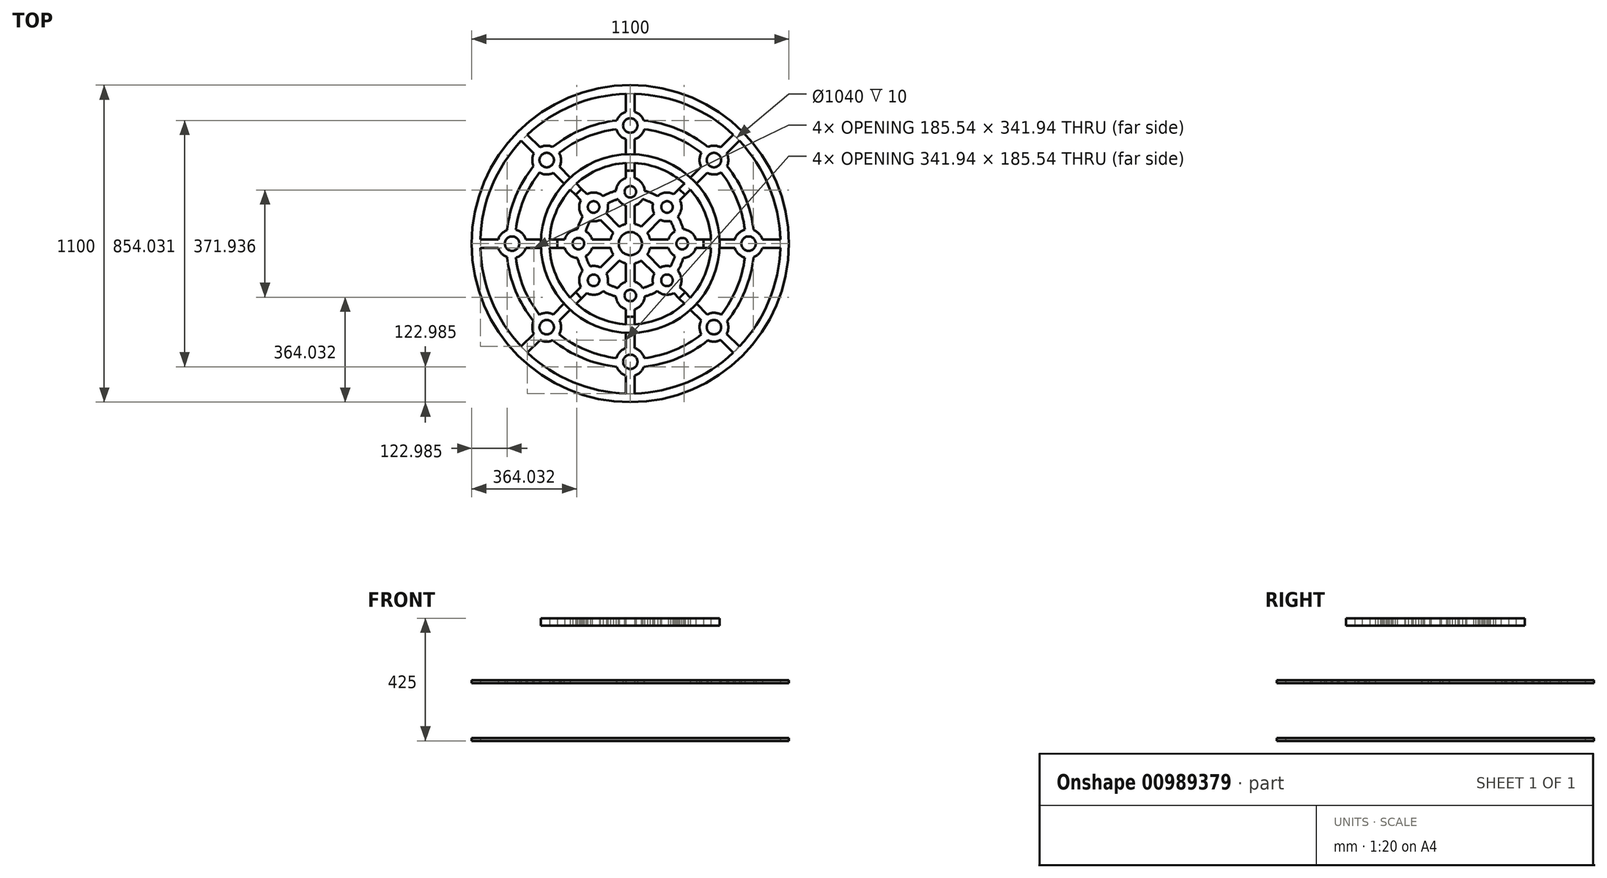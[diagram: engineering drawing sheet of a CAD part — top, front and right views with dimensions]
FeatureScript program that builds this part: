
annotation { "Feature Type Name" : "Feature", "Feature Type Description" : "" }
export const myFeature = defineFeature(function(context is Context, id is Id, definition is map)
    precondition{}
    {
        {
            var Q0;
            Q0=qCreatedBy(makeId("Top.planeOp"),FACE);
            cPlane(context, id + "F0", {"entities" : qUnion([Q0]), "cplaneType" : CPlaneType.OFFSET, "offset" : 200 * mm, "width" : 150 * mm, "height" : 150 * mm});
        }
        {
            var Q0;
            Q0=qCreatedBy(makeId("Top.planeOp"),FACE);
            cPlane(context, id + "F1", {"entities" : qUnion([Q0]), "cplaneType" : CPlaneType.OFFSET, "offset" : 200 * mm, "oppositeDirection" : true, "width" : 150 * mm, "height" : 150 * mm});
        }
        {
            var Q0;
            Q0=qCreatedBy(makeId("Top.planeOp"),FACE);
            var sketch = newSketch(context, id + "F2", { "sketchPlane" : qUnion([Q0])});
            skCircle(sketch, "E0", {"center": v(0, 0) * mm, "radius": 550 * mm});
            skArc(sketch, "E1", {"start": v(15, -519.78) * mm, "mid": v(199, -480.42) * mm, "end": v(356.94, -378.15) * mm});
            skArc(sketch, "E2", {"start": v(46.86, -427.44) * mm, "mid": v(164.55, -397.27) * mm, "end": v(269.1, -335.38) * mm});
            skArc(sketch, "E3", {"start": v(48.3, -397.07) * mm, "mid": v(153.07, -369.55) * mm, "end": v(246.62, -314.93) * mm});
            skArc(sketch, "E4", {"start": v(15, -309.64) * mm, "mid": v(118.63, -286.4) * mm, "end": v(208.34, -229.55) * mm});
            skCircle(sketch, "E5", {"center": v(0, 0) * mm, "radius": 280 * mm});
            skCircle(sketch, "E6", {"center": v(0, 0) * mm, "radius": 190 * mm, "construction": true});
            skCircle(sketch, "E7", {"center": v(0, 0) * mm, "radius": 160 * mm, "construction": true});
            skCircle(sketch, "E8", {"center": v(0, 0) * mm, "radius": 40 * mm, "construction": true});
            skCircle(sketch, "E9", {"center": v(0, 0) * mm, "radius": 70 * mm, "construction": true});
            skLineSegment(sketch, "E10", {"start": v(0, 725.48) * mm, "end": v(0, -722.46) * mm, "construction": true});
            skLineSegment(sketch, "E11", {"start": v(-695.44, 0) * mm, "end": v(901.66, 0) * mm, "construction": true});
            skArc(sketch, "E12", {"start": v(-15, -362.3) * mm, "mid": v(-36.11, -375.42) * mm, "end": v(-48.3, -397.07) * mm});
            skCircle(sketch, "E13", {"center": v(0, -410) * mm, "radius": 25 * mm});
            skLineSegment(sketch, "E14", {"start": v(15, -519.78) * mm, "end": v(15, -457.7) * mm});
            skLineSegment(sketch, "E15", {"start": v(-15, -457.7) * mm, "end": v(-15, -519.78) * mm});
            skLineSegment(sketch, "E16", {"start": v(-15, -362.3) * mm, "end": v(-15, -309.64) * mm});
            skLineSegment(sketch, "E17", {"start": v(15, -362.3) * mm, "end": v(15, -309.64) * mm});
            skArc(sketch, "E18.trimOffspring", {"start": v(-46.86, -427.44) * mm, "mid": v(-34.43, -446.26) * mm, "end": v(-15, -457.7) * mm});
            skArc(sketch, "E19.trimOffspring", {"start": v(48.3, -397.07) * mm, "mid": v(36.11, -375.42) * mm, "end": v(15, -362.3) * mm});
            skArc(sketch, "E20.trimOffspring", {"start": v(15, -457.7) * mm, "mid": v(34.43, -446.26) * mm, "end": v(46.86, -427.44) * mm});
            skArc(sketch, "E21.1.0", {"start": v(334.25, -313.03) * mm, "mid": v(339.9, -291.2) * mm, "end": v(335.38, -269.1) * mm});
            skCircle(sketch, "E21.1.1", {"center": v(289.91, -289.91) * mm, "radius": 25 * mm});
            skLineSegment(sketch, "E21.1.2", {"start": v(266.8, -245.58) * mm, "end": v(229.55, -208.34) * mm});
            skLineSegment(sketch, "E21.1.3", {"start": v(245.58, -266.8) * mm, "end": v(208.34, -229.55) * mm});
            skArc(sketch, "E21.1.4", {"start": v(245.58, -266.8) * mm, "mid": v(239.93, -291) * mm, "end": v(246.62, -314.93) * mm});
            skArc(sketch, "E21.1.5", {"start": v(269.1, -335.38) * mm, "mid": v(291.2, -339.9) * mm, "end": v(313.03, -334.25) * mm});
            skArc(sketch, "E21.1.6", {"start": v(314.93, -246.62) * mm, "mid": v(291, -239.93) * mm, "end": v(266.8, -245.58) * mm});
            skLineSegment(sketch, "E21.1.7", {"start": v(378.15, -356.94) * mm, "end": v(334.25, -313.03) * mm});
            skLineSegment(sketch, "E21.1.8", {"start": v(313.03, -334.25) * mm, "end": v(356.94, -378.15) * mm});
            skArc(sketch, "E21.2.0", {"start": v(457.7, 15) * mm, "mid": v(446.26, 34.43) * mm, "end": v(427.44, 46.86) * mm});
            skCircle(sketch, "E21.2.1", {"center": v(410, 0) * mm, "radius": 25 * mm});
            skLineSegment(sketch, "E21.2.2", {"start": v(362.3, 15) * mm, "end": v(309.64, 15) * mm});
            skLineSegment(sketch, "E21.2.3", {"start": v(362.3, -15) * mm, "end": v(309.64, -15) * mm});
            skArc(sketch, "E21.2.4", {"start": v(362.3, -15) * mm, "mid": v(375.42, -36.11) * mm, "end": v(397.07, -48.3) * mm});
            skArc(sketch, "E21.2.5", {"start": v(427.44, -46.86) * mm, "mid": v(446.26, -34.43) * mm, "end": v(457.7, -15) * mm});
            skArc(sketch, "E21.2.6", {"start": v(397.07, 48.3) * mm, "mid": v(375.42, 36.11) * mm, "end": v(362.3, 15) * mm});
            skLineSegment(sketch, "E21.2.7", {"start": v(519.78, 15) * mm, "end": v(457.7, 15) * mm});
            skLineSegment(sketch, "E21.2.8", {"start": v(457.7, -15) * mm, "end": v(519.78, -15) * mm});
            skArc(sketch, "E21.3.0", {"start": v(313.03, 334.25) * mm, "mid": v(291.2, 339.9) * mm, "end": v(269.1, 335.38) * mm});
            skCircle(sketch, "E21.3.1", {"center": v(289.91, 289.91) * mm, "radius": 25 * mm});
            skLineSegment(sketch, "E21.3.2", {"start": v(245.58, 266.8) * mm, "end": v(208.34, 229.55) * mm});
            skLineSegment(sketch, "E21.3.3", {"start": v(266.8, 245.58) * mm, "end": v(229.55, 208.34) * mm});
            skArc(sketch, "E21.3.4", {"start": v(266.8, 245.58) * mm, "mid": v(291, 239.93) * mm, "end": v(314.93, 246.62) * mm});
            skArc(sketch, "E21.3.5", {"start": v(335.38, 269.1) * mm, "mid": v(339.9, 291.2) * mm, "end": v(334.25, 313.03) * mm});
            skArc(sketch, "E21.3.6", {"start": v(246.62, 314.93) * mm, "mid": v(239.93, 291) * mm, "end": v(245.58, 266.8) * mm});
            skLineSegment(sketch, "E21.3.7", {"start": v(356.94, 378.15) * mm, "end": v(313.03, 334.25) * mm});
            skLineSegment(sketch, "E21.3.8", {"start": v(334.25, 313.03) * mm, "end": v(378.15, 356.94) * mm});
            skArc(sketch, "E21.4.0", {"start": v(-15, 457.7) * mm, "mid": v(-34.43, 446.26) * mm, "end": v(-46.86, 427.44) * mm});
            skCircle(sketch, "E21.4.1", {"center": v(0, 410) * mm, "radius": 25 * mm});
            skLineSegment(sketch, "E21.4.2", {"start": v(-15, 362.3) * mm, "end": v(-15, 309.64) * mm});
            skLineSegment(sketch, "E21.4.3", {"start": v(15, 362.3) * mm, "end": v(15, 309.64) * mm});
            skArc(sketch, "E21.4.4", {"start": v(15, 362.3) * mm, "mid": v(36.11, 375.42) * mm, "end": v(48.3, 397.07) * mm});
            skArc(sketch, "E21.4.5", {"start": v(46.86, 427.44) * mm, "mid": v(34.43, 446.26) * mm, "end": v(15, 457.7) * mm});
            skArc(sketch, "E21.4.6", {"start": v(-48.3, 397.07) * mm, "mid": v(-36.11, 375.42) * mm, "end": v(-15, 362.3) * mm});
            skLineSegment(sketch, "E21.4.7", {"start": v(-15, 519.78) * mm, "end": v(-15, 457.7) * mm});
            skLineSegment(sketch, "E21.4.8", {"start": v(15, 457.7) * mm, "end": v(15, 519.78) * mm});
            skArc(sketch, "E21.5.0", {"start": v(-334.25, 313.03) * mm, "mid": v(-339.9, 291.2) * mm, "end": v(-335.38, 269.1) * mm});
            skCircle(sketch, "E21.5.1", {"center": v(-289.91, 289.91) * mm, "radius": 25 * mm});
            skLineSegment(sketch, "E21.5.2", {"start": v(-266.8, 245.58) * mm, "end": v(-229.55, 208.34) * mm});
            skLineSegment(sketch, "E21.5.3", {"start": v(-245.58, 266.8) * mm, "end": v(-208.34, 229.55) * mm});
            skArc(sketch, "E21.5.4", {"start": v(-245.58, 266.8) * mm, "mid": v(-239.93, 291) * mm, "end": v(-246.62, 314.93) * mm});
            skArc(sketch, "E21.5.5", {"start": v(-269.1, 335.38) * mm, "mid": v(-291.2, 339.9) * mm, "end": v(-313.03, 334.25) * mm});
            skArc(sketch, "E21.5.6", {"start": v(-314.93, 246.62) * mm, "mid": v(-291, 239.93) * mm, "end": v(-266.8, 245.58) * mm});
            skLineSegment(sketch, "E21.5.7", {"start": v(-378.15, 356.94) * mm, "end": v(-334.25, 313.03) * mm});
            skLineSegment(sketch, "E21.5.8", {"start": v(-313.03, 334.25) * mm, "end": v(-356.94, 378.15) * mm});
            skArc(sketch, "E21.6.0", {"start": v(-457.7, -15) * mm, "mid": v(-446.26, -34.43) * mm, "end": v(-427.44, -46.86) * mm});
            skCircle(sketch, "E21.6.1", {"center": v(-410, 0) * mm, "radius": 25 * mm});
            skLineSegment(sketch, "E21.6.2", {"start": v(-362.3, -15) * mm, "end": v(-309.64, -15) * mm});
            skLineSegment(sketch, "E21.6.3", {"start": v(-362.3, 15) * mm, "end": v(-309.64, 15) * mm});
            skArc(sketch, "E21.6.4", {"start": v(-362.3, 15) * mm, "mid": v(-375.42, 36.11) * mm, "end": v(-397.07, 48.3) * mm});
            skArc(sketch, "E21.6.5", {"start": v(-427.44, 46.86) * mm, "mid": v(-446.26, 34.43) * mm, "end": v(-457.7, 15) * mm});
            skArc(sketch, "E21.6.6", {"start": v(-397.07, -48.3) * mm, "mid": v(-375.42, -36.11) * mm, "end": v(-362.3, -15) * mm});
            skLineSegment(sketch, "E21.6.7", {"start": v(-519.78, -15) * mm, "end": v(-457.7, -15) * mm});
            skLineSegment(sketch, "E21.6.8", {"start": v(-457.7, 15) * mm, "end": v(-519.78, 15) * mm});
            skArc(sketch, "E21.7.0", {"start": v(-313.03, -334.25) * mm, "mid": v(-291.2, -339.9) * mm, "end": v(-269.1, -335.38) * mm});
            skCircle(sketch, "E21.7.1", {"center": v(-289.91, -289.91) * mm, "radius": 25 * mm});
            skLineSegment(sketch, "E21.7.2", {"start": v(-245.58, -266.8) * mm, "end": v(-208.34, -229.55) * mm});
            skLineSegment(sketch, "E21.7.3", {"start": v(-266.8, -245.58) * mm, "end": v(-229.55, -208.34) * mm});
            skArc(sketch, "E21.7.4", {"start": v(-266.8, -245.58) * mm, "mid": v(-291, -239.93) * mm, "end": v(-314.93, -246.62) * mm});
            skArc(sketch, "E21.7.5", {"start": v(-335.38, -269.1) * mm, "mid": v(-339.9, -291.2) * mm, "end": v(-334.25, -313.03) * mm});
            skArc(sketch, "E21.7.6", {"start": v(-246.62, -314.93) * mm, "mid": v(-239.93, -291) * mm, "end": v(-245.58, -266.8) * mm});
            skLineSegment(sketch, "E21.7.7", {"start": v(-356.94, -378.15) * mm, "end": v(-313.03, -334.25) * mm});
            skLineSegment(sketch, "E21.7.8", {"start": v(-334.25, -313.03) * mm, "end": v(-378.15, -356.94) * mm});
            skArc(sketch, "E22.trimOffspring", {"start": v(-246.62, -314.93) * mm, "mid": v(-153.07, -369.55) * mm, "end": v(-48.3, -397.07) * mm});
            skArc(sketch, "E23.trimOffspring", {"start": v(-269.1, -335.38) * mm, "mid": v(-164.55, -397.27) * mm, "end": v(-46.86, -427.44) * mm});
            skArc(sketch, "E24.trimOffspring", {"start": v(-356.94, -378.15) * mm, "mid": v(-199, -480.42) * mm, "end": v(-15, -519.78) * mm});
            skArc(sketch, "E25.trimOffspring", {"start": v(-208.34, -229.55) * mm, "mid": v(-118.63, -286.4) * mm, "end": v(-15, -309.64) * mm});
            skArc(sketch, "E26.trimOffspring", {"start": v(-397.07, -48.3) * mm, "mid": v(-369.55, -153.07) * mm, "end": v(-314.93, -246.62) * mm});
            skArc(sketch, "E27.trimOffspring", {"start": v(-427.44, -46.86) * mm, "mid": v(-397.27, -164.55) * mm, "end": v(-335.38, -269.1) * mm});
            skArc(sketch, "E28.trimOffspring", {"start": v(-309.64, -15) * mm, "mid": v(-286.4, -118.63) * mm, "end": v(-229.55, -208.34) * mm});
            skArc(sketch, "E29.trimOffspring", {"start": v(-519.78, -15) * mm, "mid": v(-480.42, -199) * mm, "end": v(-378.15, -356.94) * mm});
            skArc(sketch, "E30.trimOffspring", {"start": v(-314.93, 246.62) * mm, "mid": v(-369.55, 153.07) * mm, "end": v(-397.07, 48.3) * mm});
            skArc(sketch, "E31.trimOffspring", {"start": v(-335.38, 269.1) * mm, "mid": v(-397.27, 164.55) * mm, "end": v(-427.44, 46.86) * mm});
            skArc(sketch, "E32.trimOffspring", {"start": v(-378.15, 356.94) * mm, "mid": v(-480.42, 199) * mm, "end": v(-519.78, 15) * mm});
            skArc(sketch, "E33.trimOffspring", {"start": v(-229.55, 208.34) * mm, "mid": v(-286.4, 118.63) * mm, "end": v(-309.64, 15) * mm});
            skArc(sketch, "E34.trimOffspring", {"start": v(-15, 309.64) * mm, "mid": v(-118.63, 286.4) * mm, "end": v(-208.34, 229.55) * mm});
            skArc(sketch, "E35.trimOffspring", {"start": v(-48.3, 397.07) * mm, "mid": v(-153.07, 369.55) * mm, "end": v(-246.62, 314.93) * mm});
            skArc(sketch, "E36.trimOffspring", {"start": v(-46.86, 427.44) * mm, "mid": v(-164.55, 397.27) * mm, "end": v(-269.1, 335.38) * mm});
            skArc(sketch, "E37.trimOffspring", {"start": v(-15, 519.78) * mm, "mid": v(-199, 480.42) * mm, "end": v(-356.94, 378.15) * mm});
            skArc(sketch, "E38.trimOffspring", {"start": v(269.1, 335.38) * mm, "mid": v(164.55, 397.27) * mm, "end": v(46.86, 427.44) * mm});
            skArc(sketch, "E39.trimOffspring", {"start": v(246.62, 314.93) * mm, "mid": v(153.07, 369.55) * mm, "end": v(48.3, 397.07) * mm});
            skArc(sketch, "E40.trimOffspring", {"start": v(208.34, 229.55) * mm, "mid": v(118.63, 286.4) * mm, "end": v(15, 309.64) * mm});
            skArc(sketch, "E41.trimOffspring", {"start": v(356.94, 378.15) * mm, "mid": v(199, 480.42) * mm, "end": v(15, 519.78) * mm});
            skArc(sketch, "E42.trimOffspring", {"start": v(309.64, 15) * mm, "mid": v(286.4, 118.63) * mm, "end": v(229.55, 208.34) * mm});
            skArc(sketch, "E43.trimOffspring", {"start": v(397.07, 48.3) * mm, "mid": v(369.55, 153.07) * mm, "end": v(314.93, 246.62) * mm});
            skArc(sketch, "E44.trimOffspring", {"start": v(427.44, 46.86) * mm, "mid": v(397.27, 164.55) * mm, "end": v(335.38, 269.1) * mm});
            skArc(sketch, "E45.trimOffspring", {"start": v(519.78, 15) * mm, "mid": v(480.42, 199) * mm, "end": v(378.15, 356.94) * mm});
            skArc(sketch, "E46.trimOffspring", {"start": v(335.38, -269.1) * mm, "mid": v(397.27, -164.55) * mm, "end": v(427.44, -46.86) * mm});
            skArc(sketch, "E47.trimOffspring", {"start": v(314.93, -246.62) * mm, "mid": v(369.55, -153.07) * mm, "end": v(397.07, -48.3) * mm});
            skArc(sketch, "E48.trimOffspring", {"start": v(378.15, -356.94) * mm, "mid": v(480.42, -199) * mm, "end": v(519.78, -15) * mm});
            skArc(sketch, "E49.trimOffspring", {"start": v(229.55, -208.34) * mm, "mid": v(286.4, -118.63) * mm, "end": v(309.64, -15) * mm});
            skSolve(sketch);
        }
        {
            var Q0;
            Q0 = qSketchRegion(id + "F2", true);
            extrude(context, id + "F3", {"entities" : qUnion([Q0]), "depth" : 10 * mm, "offsetDistance" : 25 * mm});
        }
        {
            var Q0;
            Q0=qCreatedBy(id+"F0.planeOp",FACE);
            var sketch = newSketch(context, id + "F4", { "sketchPlane" : qUnion([Q0])});
            skArc(sketch, "E50.0", {"start": v(42.8, -154.17) * mm, "mid": v(61.23, -147.82) * mm, "end": v(78.74, -139.28) * mm});
            skArc(sketch, "E51.0", {"start": v(49.89, -183.33) * mm, "mid": v(72.7, -175.54) * mm, "end": v(94.36, -164.91) * mm});
            skArc(sketch, "E52.0", {"start": v(15, -279.6) * mm, "mid": v(107.15, -258.69) * mm, "end": v(187.1, -208.31) * mm});
            skArc(sketch, "E53.0", {"start": v(15, -68.37) * mm, "mid": v(26.79, -64.67) * mm, "end": v(37.74, -58.95) * mm});
            skCircle(sketch, "E54.0", {"center": v(0, 0) * mm, "radius": 40 * mm});
            skPoint(sketch, "E55.0", {"position": v(15, 309.64) * mm});
            skCircle(sketch, "E56", {"center": v(0, 0) * mm, "radius": 310 * mm});
            skArc(sketch, "E57", {"start": v(-15, -132.3) * mm, "mid": v(-30.9, -140.7) * mm, "end": v(-42.8, -154.17) * mm});
            skCircle(sketch, "E58", {"center": v(0, -180) * mm, "radius": 20 * mm});
            skLineSegment(sketch, "E59", {"start": v(-15, -68.37) * mm, "end": v(-15, -132.3) * mm});
            skLineSegment(sketch, "E60", {"start": v(15, -68.37) * mm, "end": v(15, -132.3) * mm});
            skLineSegment(sketch, "E61", {"start": v(-15, -227.7) * mm, "end": v(-15, -279.6) * mm});
            skLineSegment(sketch, "E62", {"start": v(15, -227.7) * mm, "end": v(15, -279.6) * mm});
            skArc(sketch, "E63.trimOffspring", {"start": v(42.8, -154.17) * mm, "mid": v(30.9, -140.7) * mm, "end": v(15, -132.3) * mm});
            skArc(sketch, "E64.trimOffspring", {"start": v(15, -227.7) * mm, "mid": v(39.3, -210.9) * mm, "end": v(49.89, -183.33) * mm});
            skArc(sketch, "E65.trimOffspring", {"start": v(-49.89, -183.33) * mm, "mid": v(-39.3, -210.9) * mm, "end": v(-15, -227.7) * mm});
            skLineSegment(sketch, "E66.1.0", {"start": v(58.95, -37.74) * mm, "end": v(104.16, -82.95) * mm});
            skLineSegment(sketch, "E66.1.1", {"start": v(37.74, -58.95) * mm, "end": v(82.95, -104.16) * mm});
            skArc(sketch, "E66.1.2", {"start": v(82.95, -104.16) * mm, "mid": v(77.63, -121.34) * mm, "end": v(78.74, -139.28) * mm});
            skCircle(sketch, "E66.1.3", {"center": v(127.28, -127.28) * mm, "radius": 20 * mm});
            skArc(sketch, "E66.1.4", {"start": v(94.36, -164.91) * mm, "mid": v(121.34, -176.93) * mm, "end": v(150.4, -171.61) * mm});
            skArc(sketch, "E66.1.5", {"start": v(171.61, -150.4) * mm, "mid": v(176.93, -121.34) * mm, "end": v(164.91, -94.36) * mm});
            skArc(sketch, "E66.1.6", {"start": v(139.28, -78.74) * mm, "mid": v(121.34, -77.63) * mm, "end": v(104.16, -82.95) * mm});
            skLineSegment(sketch, "E66.1.7", {"start": v(171.61, -150.4) * mm, "end": v(208.31, -187.1) * mm});
            skLineSegment(sketch, "E66.1.8", {"start": v(150.4, -171.61) * mm, "end": v(187.1, -208.31) * mm});
            skLineSegment(sketch, "E66.2.0", {"start": v(68.37, 15) * mm, "end": v(132.3, 15) * mm});
            skLineSegment(sketch, "E66.2.1", {"start": v(68.37, -15) * mm, "end": v(132.3, -15) * mm});
            skArc(sketch, "E66.2.2", {"start": v(132.3, -15) * mm, "mid": v(140.7, -30.9) * mm, "end": v(154.17, -42.8) * mm});
            skCircle(sketch, "E66.2.3", {"center": v(180, 0) * mm, "radius": 20 * mm});
            skArc(sketch, "E66.2.4", {"start": v(183.33, -49.89) * mm, "mid": v(210.9, -39.3) * mm, "end": v(227.7, -15) * mm});
            skArc(sketch, "E66.2.5", {"start": v(227.7, 15) * mm, "mid": v(210.9, 39.3) * mm, "end": v(183.33, 49.89) * mm});
            skArc(sketch, "E66.2.6", {"start": v(154.17, 42.8) * mm, "mid": v(140.7, 30.9) * mm, "end": v(132.3, 15) * mm});
            skLineSegment(sketch, "E66.2.7", {"start": v(227.7, 15) * mm, "end": v(279.6, 15) * mm});
            skLineSegment(sketch, "E66.2.8", {"start": v(227.7, -15) * mm, "end": v(279.6, -15) * mm});
            skLineSegment(sketch, "E66.3.0", {"start": v(37.74, 58.95) * mm, "end": v(82.95, 104.16) * mm});
            skLineSegment(sketch, "E66.3.1", {"start": v(58.95, 37.74) * mm, "end": v(104.16, 82.95) * mm});
            skArc(sketch, "E66.3.2", {"start": v(104.16, 82.95) * mm, "mid": v(121.34, 77.63) * mm, "end": v(139.28, 78.74) * mm});
            skCircle(sketch, "E66.3.3", {"center": v(127.28, 127.28) * mm, "radius": 20 * mm});
            skArc(sketch, "E66.3.4", {"start": v(164.91, 94.36) * mm, "mid": v(176.93, 121.34) * mm, "end": v(171.61, 150.4) * mm});
            skArc(sketch, "E66.3.5", {"start": v(150.4, 171.61) * mm, "mid": v(121.34, 176.93) * mm, "end": v(94.36, 164.91) * mm});
            skArc(sketch, "E66.3.6", {"start": v(78.74, 139.28) * mm, "mid": v(77.63, 121.34) * mm, "end": v(82.95, 104.16) * mm});
            skLineSegment(sketch, "E66.3.7", {"start": v(150.4, 171.61) * mm, "end": v(187.1, 208.31) * mm});
            skLineSegment(sketch, "E66.3.8", {"start": v(171.61, 150.4) * mm, "end": v(208.31, 187.1) * mm});
            skLineSegment(sketch, "E66.4.0", {"start": v(-15, 68.37) * mm, "end": v(-15, 132.3) * mm});
            skLineSegment(sketch, "E66.4.1", {"start": v(15, 68.37) * mm, "end": v(15, 132.3) * mm});
            skArc(sketch, "E66.4.2", {"start": v(15, 132.3) * mm, "mid": v(30.9, 140.7) * mm, "end": v(42.8, 154.17) * mm});
            skCircle(sketch, "E66.4.3", {"center": v(0, 180) * mm, "radius": 20 * mm});
            skArc(sketch, "E66.4.4", {"start": v(49.89, 183.33) * mm, "mid": v(39.3, 210.9) * mm, "end": v(15, 227.7) * mm});
            skArc(sketch, "E66.4.5", {"start": v(-15, 227.7) * mm, "mid": v(-39.3, 210.9) * mm, "end": v(-49.89, 183.33) * mm});
            skArc(sketch, "E66.4.6", {"start": v(-42.8, 154.17) * mm, "mid": v(-30.9, 140.7) * mm, "end": v(-15, 132.3) * mm});
            skLineSegment(sketch, "E66.4.7", {"start": v(-15, 227.7) * mm, "end": v(-15, 279.6) * mm});
            skLineSegment(sketch, "E66.4.8", {"start": v(15, 227.7) * mm, "end": v(15, 279.6) * mm});
            skLineSegment(sketch, "E66.5.0", {"start": v(-58.95, 37.74) * mm, "end": v(-104.16, 82.95) * mm});
            skLineSegment(sketch, "E66.5.1", {"start": v(-37.74, 58.95) * mm, "end": v(-82.95, 104.16) * mm});
            skArc(sketch, "E66.5.2", {"start": v(-82.95, 104.16) * mm, "mid": v(-77.63, 121.34) * mm, "end": v(-78.74, 139.28) * mm});
            skCircle(sketch, "E66.5.3", {"center": v(-127.28, 127.28) * mm, "radius": 20 * mm});
            skArc(sketch, "E66.5.4", {"start": v(-94.36, 164.91) * mm, "mid": v(-121.34, 176.93) * mm, "end": v(-150.4, 171.61) * mm});
            skArc(sketch, "E66.5.5", {"start": v(-171.61, 150.4) * mm, "mid": v(-176.93, 121.34) * mm, "end": v(-164.91, 94.36) * mm});
            skArc(sketch, "E66.5.6", {"start": v(-139.28, 78.74) * mm, "mid": v(-121.34, 77.63) * mm, "end": v(-104.16, 82.95) * mm});
            skLineSegment(sketch, "E66.5.7", {"start": v(-171.61, 150.4) * mm, "end": v(-208.31, 187.1) * mm});
            skLineSegment(sketch, "E66.5.8", {"start": v(-150.4, 171.61) * mm, "end": v(-187.1, 208.31) * mm});
            skLineSegment(sketch, "E66.6.0", {"start": v(-68.37, -15) * mm, "end": v(-132.3, -15) * mm});
            skLineSegment(sketch, "E66.6.1", {"start": v(-68.37, 15) * mm, "end": v(-132.3, 15) * mm});
            skArc(sketch, "E66.6.2", {"start": v(-132.3, 15) * mm, "mid": v(-140.7, 30.9) * mm, "end": v(-154.17, 42.8) * mm});
            skCircle(sketch, "E66.6.3", {"center": v(-180, 0) * mm, "radius": 20 * mm});
            skArc(sketch, "E66.6.4", {"start": v(-183.33, 49.89) * mm, "mid": v(-210.9, 39.3) * mm, "end": v(-227.7, 15) * mm});
            skArc(sketch, "E66.6.5", {"start": v(-227.7, -15) * mm, "mid": v(-210.9, -39.3) * mm, "end": v(-183.33, -49.89) * mm});
            skArc(sketch, "E66.6.6", {"start": v(-154.17, -42.8) * mm, "mid": v(-140.7, -30.9) * mm, "end": v(-132.3, -15) * mm});
            skLineSegment(sketch, "E66.6.7", {"start": v(-227.7, -15) * mm, "end": v(-279.6, -15) * mm});
            skLineSegment(sketch, "E66.6.8", {"start": v(-227.7, 15) * mm, "end": v(-279.6, 15) * mm});
            skLineSegment(sketch, "E66.7.0", {"start": v(-37.74, -58.95) * mm, "end": v(-82.95, -104.16) * mm});
            skLineSegment(sketch, "E66.7.1", {"start": v(-58.95, -37.74) * mm, "end": v(-104.16, -82.95) * mm});
            skArc(sketch, "E66.7.2", {"start": v(-104.16, -82.95) * mm, "mid": v(-121.34, -77.63) * mm, "end": v(-139.28, -78.74) * mm});
            skCircle(sketch, "E66.7.3", {"center": v(-127.28, -127.28) * mm, "radius": 20 * mm});
            skArc(sketch, "E66.7.4", {"start": v(-164.91, -94.36) * mm, "mid": v(-176.93, -121.34) * mm, "end": v(-171.61, -150.4) * mm});
            skArc(sketch, "E66.7.5", {"start": v(-150.4, -171.61) * mm, "mid": v(-121.34, -176.93) * mm, "end": v(-94.36, -164.91) * mm});
            skArc(sketch, "E66.7.6", {"start": v(-78.74, -139.28) * mm, "mid": v(-77.63, -121.34) * mm, "end": v(-82.95, -104.16) * mm});
            skLineSegment(sketch, "E66.7.7", {"start": v(-150.4, -171.61) * mm, "end": v(-187.1, -208.31) * mm});
            skLineSegment(sketch, "E66.7.8", {"start": v(-171.61, -150.4) * mm, "end": v(-208.31, -187.1) * mm});
            skArc(sketch, "E67.trimOffspring", {"start": v(-94.36, -164.91) * mm, "mid": v(-72.7, -175.54) * mm, "end": v(-49.89, -183.33) * mm});
            skArc(sketch, "E68.trimOffspring", {"start": v(-78.74, -139.28) * mm, "mid": v(-61.23, -147.82) * mm, "end": v(-42.8, -154.17) * mm});
            skArc(sketch, "E69.trimOffspring", {"start": v(-187.1, -208.31) * mm, "mid": v(-107.15, -258.69) * mm, "end": v(-15, -279.6) * mm});
            skArc(sketch, "E70.trimOffspring", {"start": v(-37.74, -58.95) * mm, "mid": v(-26.79, -64.67) * mm, "end": v(-15, -68.37) * mm});
            skArc(sketch, "E71.trimOffspring", {"start": v(-68.37, -15) * mm, "mid": v(-64.67, -26.79) * mm, "end": v(-58.95, -37.74) * mm});
            skArc(sketch, "E72.trimOffspring", {"start": v(-154.17, -42.8) * mm, "mid": v(-147.82, -61.23) * mm, "end": v(-139.28, -78.74) * mm});
            skArc(sketch, "E73.trimOffspring", {"start": v(-183.33, -49.89) * mm, "mid": v(-175.54, -72.7) * mm, "end": v(-164.91, -94.36) * mm});
            skArc(sketch, "E74.trimOffspring", {"start": v(-279.6, -15) * mm, "mid": v(-258.69, -107.15) * mm, "end": v(-208.31, -187.1) * mm});
            skArc(sketch, "E75.trimOffspring", {"start": v(-164.91, 94.36) * mm, "mid": v(-175.54, 72.7) * mm, "end": v(-183.33, 49.89) * mm});
            skArc(sketch, "E76.trimOffspring", {"start": v(-139.28, 78.74) * mm, "mid": v(-147.82, 61.23) * mm, "end": v(-154.17, 42.8) * mm});
            skArc(sketch, "E77.trimOffspring", {"start": v(-208.31, 187.1) * mm, "mid": v(-258.69, 107.15) * mm, "end": v(-279.6, 15) * mm});
            skArc(sketch, "E78.trimOffspring", {"start": v(-58.95, 37.74) * mm, "mid": v(-64.67, 26.79) * mm, "end": v(-68.37, 15) * mm});
            skArc(sketch, "E79.trimOffspring", {"start": v(-15, 68.37) * mm, "mid": v(-26.79, 64.67) * mm, "end": v(-37.74, 58.95) * mm});
            skArc(sketch, "E80.trimOffspring", {"start": v(-42.8, 154.17) * mm, "mid": v(-61.23, 147.82) * mm, "end": v(-78.74, 139.28) * mm});
            skArc(sketch, "E81.trimOffspring", {"start": v(-49.89, 183.33) * mm, "mid": v(-72.7, 175.54) * mm, "end": v(-94.36, 164.91) * mm});
            skArc(sketch, "E82.trimOffspring", {"start": v(78.74, 139.28) * mm, "mid": v(61.23, 147.82) * mm, "end": v(42.8, 154.17) * mm});
            skArc(sketch, "E83.trimOffspring", {"start": v(94.36, 164.91) * mm, "mid": v(72.7, 175.54) * mm, "end": v(49.89, 183.33) * mm});
            skArc(sketch, "E84.trimOffspring", {"start": v(183.33, 49.89) * mm, "mid": v(175.54, 72.7) * mm, "end": v(164.91, 94.36) * mm});
            skArc(sketch, "E85.trimOffspring", {"start": v(154.17, 42.8) * mm, "mid": v(147.82, 61.23) * mm, "end": v(139.28, 78.74) * mm});
            skArc(sketch, "E86.trimOffspring", {"start": v(68.37, 15) * mm, "mid": v(64.67, 26.79) * mm, "end": v(58.95, 37.74) * mm});
            skArc(sketch, "E87.trimOffspring", {"start": v(279.6, 15) * mm, "mid": v(258.69, 107.15) * mm, "end": v(208.31, 187.1) * mm});
            skArc(sketch, "E88.trimOffspring", {"start": v(58.95, -37.74) * mm, "mid": v(64.67, -26.79) * mm, "end": v(68.37, -15) * mm});
            skArc(sketch, "E89.trimOffspring", {"start": v(139.28, -78.74) * mm, "mid": v(147.82, -61.23) * mm, "end": v(154.17, -42.8) * mm});
            skArc(sketch, "E90.trimOffspring", {"start": v(164.91, -94.36) * mm, "mid": v(175.54, -72.7) * mm, "end": v(183.33, -49.89) * mm});
            skArc(sketch, "E91.trimOffspring", {"start": v(208.31, -187.1) * mm, "mid": v(258.69, -107.15) * mm, "end": v(279.6, -15) * mm});
            skArc(sketch, "E92.trimOffspring", {"start": v(37.74, 58.95) * mm, "mid": v(26.79, 64.67) * mm, "end": v(15, 68.37) * mm});
            skLineSegment(sketch, "E93", {"start": v(-253.65, 15) * mm, "end": v(-253.65, -15) * mm});
            skLineSegment(sketch, "E94", {"start": v(-189.96, 168.75) * mm, "end": v(-168.75, 189.96) * mm});
            skLineSegment(sketch, "E95", {"start": v(-15, 253.65) * mm, "end": v(15, 253.65) * mm});
            skLineSegment(sketch, "E96", {"start": v(168.75, 189.96) * mm, "end": v(189.96, 168.75) * mm});
            skLineSegment(sketch, "E97", {"start": v(253.65, 15) * mm, "end": v(253.65, -15) * mm});
            skLineSegment(sketch, "E98", {"start": v(189.96, -168.75) * mm, "end": v(168.75, -189.96) * mm});
            skLineSegment(sketch, "E99", {"start": v(15, -253.65) * mm, "end": v(-15, -253.65) * mm});
            skLineSegment(sketch, "E100", {"start": v(-168.75, -189.96) * mm, "end": v(-189.96, -168.75) * mm});
            skArc(sketch, "E101.trimOffspring", {"start": v(-15, 279.6) * mm, "mid": v(-107.15, 258.69) * mm, "end": v(-187.1, 208.31) * mm});
            skArc(sketch, "E102.trimOffspring", {"start": v(187.1, 208.31) * mm, "mid": v(107.15, 258.69) * mm, "end": v(15, 279.6) * mm});
            skSolve(sketch);
        }
        {
            var Q0;
            Q0=makeQuery(id+"F4.imprint","IMPRINT",FACE,{"disambiguationData":[TD([[makeQuery(id+"F4.imprint","IMPRINT",EDGE,{"derivedFrom":sQuery(id+"F4.wireOp",EDGE,"E50.0")}),-1.0]])]});
            extrude(context, id + "F5", {"entities" : qUnion([Q0]), "depth" : 25 * mm, "offsetDistance" : 25 * mm});
        }
        {
            var Q0;
            Q0=qCreatedBy(id+"F1.planeOp",FACE);
            var sketch = newSketch(context, id + "F6", { "sketchPlane" : qUnion([Q0])});
            skCircle(sketch, "E103.0", {"center": v(0, 0) * mm, "radius": 550 * mm});
            skPoint(sketch, "E104.0", {"position": v(15, -519.78) * mm});
            skCircle(sketch, "E105", {"center": v(0, 0) * mm, "radius": 520 * mm});
            skSolve(sketch);
        }
        {
            var Q0;
            Q0 = qSketchRegion(id + "F6", true);
            extrude(context, id + "F7", {"entities" : qUnion([Q0]), "depth" : 10 * mm, "offsetDistance" : 25 * mm});
        }
        {
            var Q0;
            Q0 = qSketchRegion(id + "F4", true);
            extrude(context, id + "F8", {"entities" : qUnion([Q0]), "depth" : 25 * mm, "offsetDistance" : 25 * mm});
        }
    });
